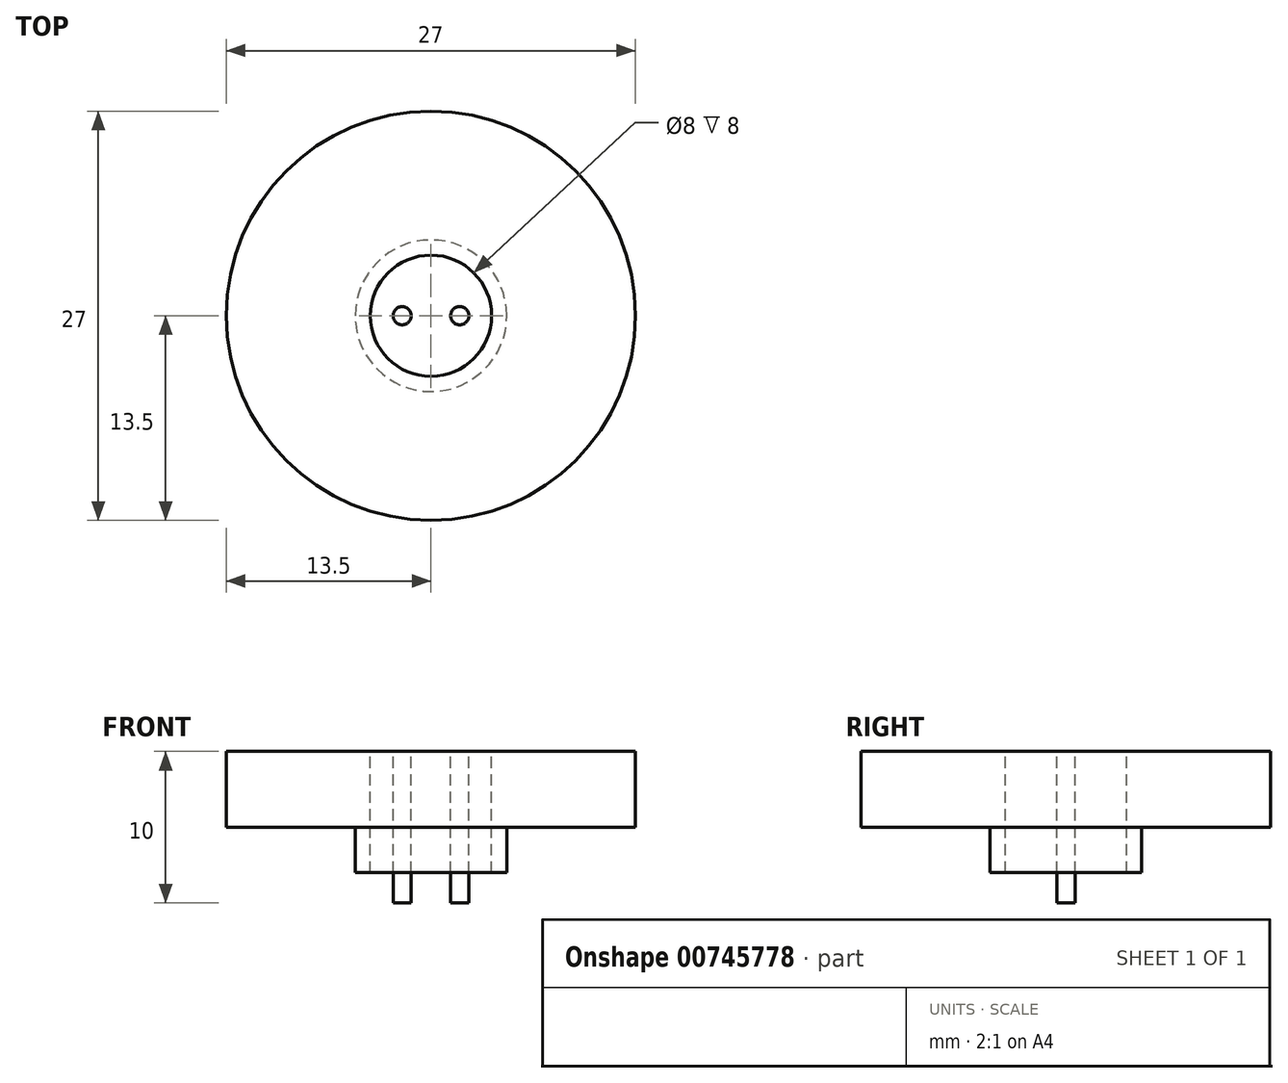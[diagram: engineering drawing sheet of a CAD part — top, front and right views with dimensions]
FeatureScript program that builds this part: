
annotation { "Feature Type Name" : "Feature", "Feature Type Description" : "" }
export const myFeature = defineFeature(function(context is Context, id is Id, definition is map)
    precondition{}
    {
        {
            var Q0;
            Q0=qCreatedBy(makeId("Top.planeOp"),FACE);
            var sketch = newSketch(context, id + "F0", { "sketchPlane" : qUnion([Q0])});
            skCircle(sketch, "E0", {"center": v(0, 0) * mm, "radius": 13.5 * mm});
            skSolve(sketch);
        }
        {
            var Q0;
            Q0 = qSketchRegion(id + "F0", true);
            extrude(context, id + "F1", {"entities" : qUnion([Q0]), "depth" : 5 * mm, "offsetDistance" : 25 * mm});
        }
        {
            var Q0;
            Q0=makeQuery(id+"F1.opExtrude","CAP_FACE",FACE,{"disambiguationData":[OSD([sQuery(id+"F0.wireOp",EDGE,"E0")])],"isStart":true});
            var sketch = newSketch(context, id + "F2", { "sketchPlane" : qUnion([Q0])});
            skCircle(sketch, "E1", {"center": v(0, 0) * mm, "radius": 5 * mm});
            skSolve(sketch);
        }
        {
            var Q0;
            Q0 = qSketchRegion(id + "F2", true);
            extrude(context, id + "F3", {"entities" : qUnion([Q0]), "operationType" : NewBodyOperationType.ADD, "depth" : 3 * mm, "offsetDistance" : 25 * mm});
        }
        {
            var Q0;
            Q0=makeQuery(id+"F1.opExtrude","CAP_FACE",FACE,{"disambiguationData":[OSD([sQuery(id+"F0.wireOp",EDGE,"E0")])],"isStart":false});
            var sketch = newSketch(context, id + "F4", { "sketchPlane" : qUnion([Q0])});
            skCircle(sketch, "E2", {"center": v(0, 0) * mm, "radius": 4 * mm});
            skSolve(sketch);
        }
        {
            var Q0;
            Q0 = qSketchRegion(id + "F4", true);
            extrude(context, id + "F5", {"entities" : qUnion([Q0]), "operationType" : NewBodyOperationType.REMOVE, "oppositeDirection" : true, "depth" : 25 * mm, "offsetDistance" : 25 * mm});
        }
        {
            var Q0;
            Q0=makeQuery(id+"F1.opExtrude","CAP_FACE",FACE,{"disambiguationData":[OSD([sQuery(id+"F0.wireOp",EDGE,"E0")])],"isStart":false});
            var sketch = newSketch(context, id + "F6", { "sketchPlane" : qUnion([Q0])});
            skCircle(sketch, "E3", {"center": v(0, 0) * mm, "radius": 4 * mm});
            skSolve(sketch);
        }
        {
            var Q0;
            Q0 = qSketchRegion(id + "F6", true);
            extrude(context, id + "F7", {"entities" : qUnion([Q0]), "oppositeDirection" : true, "depth" : 8 * mm, "offsetDistance" : 25 * mm});
        }
        {
            var Q0;
            Q0=makeQuery(id+"F7.opExtrude","CAP_FACE",FACE,{"disambiguationData":[OSD([sQuery(id+"F6.wireOp",EDGE,"E3")])],"isStart":true});
            var sketch = newSketch(context, id + "F8", { "sketchPlane" : qUnion([Q0])});
            skCircle(sketch, "E4", {"center": v(-1.9, 0) * mm, "radius": 0.6 * mm});
            skCircle(sketch, "E5", {"center": v(1.9, 0) * mm, "radius": 0.6 * mm});
            skSolve(sketch);
        }
        {
            var Q0;
            Q0 = qSketchRegion(id + "F8", true);
            extrude(context, id + "F9", {"entities" : qUnion([Q0]), "oppositeDirection" : true, "depth" : 10 * mm, "offsetDistance" : 25 * mm});
        }
    });
